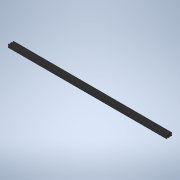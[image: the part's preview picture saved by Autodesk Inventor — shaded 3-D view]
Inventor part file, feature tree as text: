
AUTODESK INVENTOR PART (.ipt)
format: ipt  version: 2021 (Build 250183000, 183)  size: 201,728 bytes
history: native  units: mm
features: extrude x1, sketch x1
ambient origin geometry x8: Origin, YZ Plane, XZ Plane, XY Plane, X Axis, Y Axis, Z Axis, Center Point
bodies: Solid1 (feature_tree)
feature tree (2):
  extrude  "Extrusion1"  [1 undecoded]
  sketch  "Skizze_1"  dims[d0=1400.0mm d1=0.0mm]
note: 1 required parameter value undecoded (feature->parameter linkage not recoverable at this tier; creation-order binding heuristic only, values carry confidence <= 0.55)
